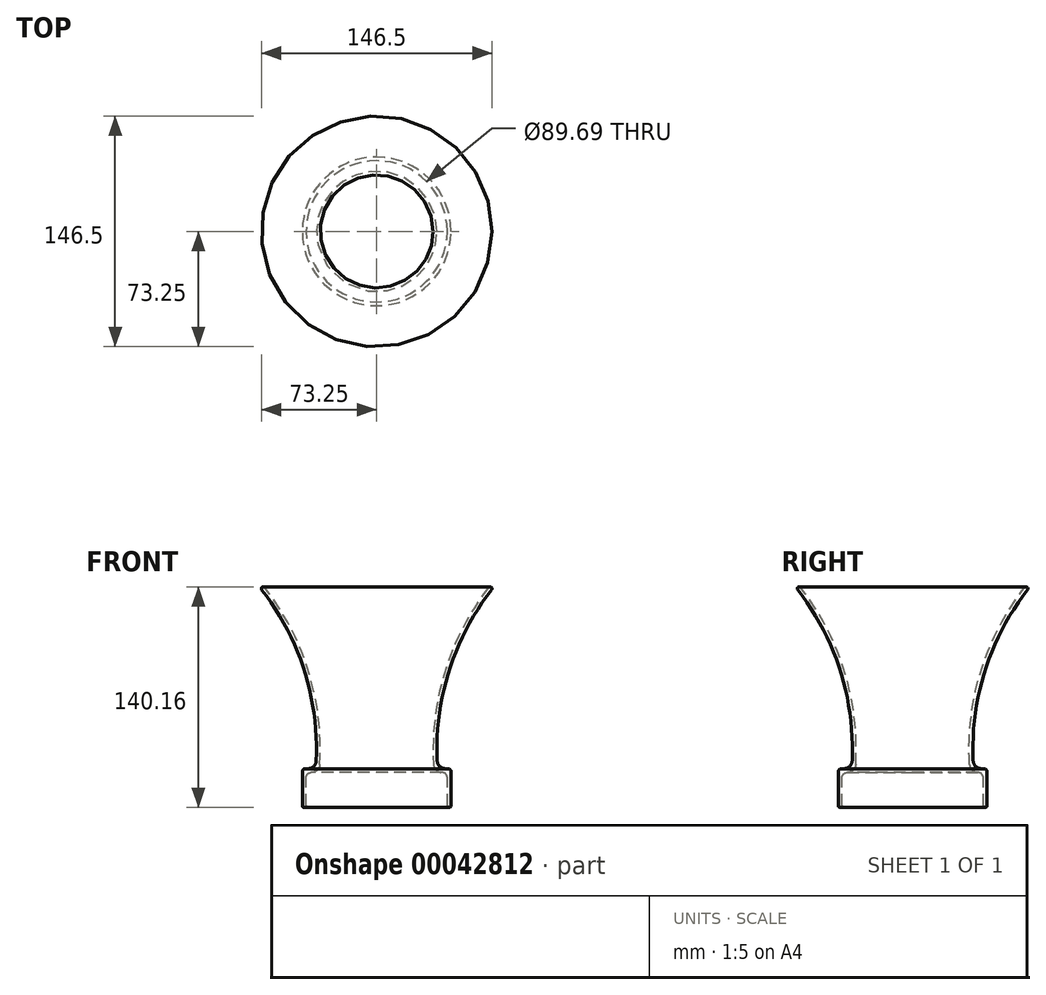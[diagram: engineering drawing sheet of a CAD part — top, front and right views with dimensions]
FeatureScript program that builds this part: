
annotation { "Feature Type Name" : "Feature", "Feature Type Description" : "" }
export const myFeature = defineFeature(function(context is Context, id is Id, definition is map)
    precondition{}
    {
        {
            var Q0;
            Q0=qCreatedBy(makeId("Front.planeOp"),FACE);
            var sketch = newSketch(context, id + "F0", { "sketchPlane" : qUnion([Q0])});
            skLineSegment(sketch, "E0", {"start": v(44.85, 1.2) * mm, "end": v(44.85, 18.92) * mm});
            skLineSegment(sketch, "E1", {"start": v(41.47, 22.23) * mm, "end": v(41.54, 22.23) * mm});
            skLineSegment(sketch, "E2", {"start": v(36.51, 22.22) * mm, "end": v(71.12, 139.7) * mm, "construction": true});
            skArc(sketch, "E3", {"start": v(71.12, 139.7) * mm, "mid": v(43.41, 86.65) * mm, "end": v(36.14, 27.25) * mm});
            skLineSegment(sketch, "E4", {"start": v(0, 74.34) * mm, "end": v(0, 0) * mm});
            skLineSegment(sketch, "E5.0", {"start": v(47.23, 1.2) * mm, "end": v(47.23, 22.7) * mm});
            skLineSegment(sketch, "E5.1", {"start": v(43.73, 24.6) * mm, "end": v(45.32, 24.6) * mm});
            skArc(sketch, "E5.2", {"start": v(73, 138.24) * mm, "mid": v(46.04, 87.05) * mm, "end": v(38.4, 29.7) * mm});
            skPoint(sketch, "E6.visualSharp", {"position": v(38.7, 24.6) * mm});
            skArc(sketch, "E6.filletArc", {"start": v(38.4, 29.7) * mm, "mid": v(40.04, 26.09) * mm, "end": v(43.73, 24.6) * mm});
            skPoint(sketch, "E7.visualSharp", {"position": v(44.85, 22.23) * mm});
            skArc(sketch, "E7.filletArc", {"start": v(44.85, 18.92) * mm, "mid": v(43.88, 21.26) * mm, "end": v(41.54, 22.23) * mm});
            skPoint(sketch, "E8.visualSharp", {"position": v(36.51, 22.23) * mm});
            skArc(sketch, "E8.filletArc", {"start": v(36.14, 27.25) * mm, "mid": v(37.8, 23.68) * mm, "end": v(41.47, 22.23) * mm});
            skArc(sketch, "E9", {"start": v(44.85, 1.2) * mm, "mid": v(46.04, 0) * mm, "end": v(47.23, 1.2) * mm});
            skArc(sketch, "E10", {"start": v(71.12, 139.7) * mm, "mid": v(72.8, 139.9) * mm, "end": v(73, 138.24) * mm});
            skPoint(sketch, "E11.visualSharp", {"position": v(47.23, 24.6) * mm});
            skArc(sketch, "E11.filletArc", {"start": v(47.23, 22.7) * mm, "mid": v(46.67, 24.05) * mm, "end": v(45.32, 24.6) * mm});
            skPoint(sketch, "E12", {"position": v(46.04, 0) * mm});
            skSolve(sketch);
        }
        {
            var Q0;
            Q0=qSketchRegion(id+"F0",true);
            var Q1;
            Q1=sQuery(id+"F0.wireOp",EDGE,"E4");
            revolve(context, id + "F1", {"entities" : qUnion([Q0]), "axis" : qUnion([Q1]), "revolveType" : RevolveType.FULL});
        }
    });
